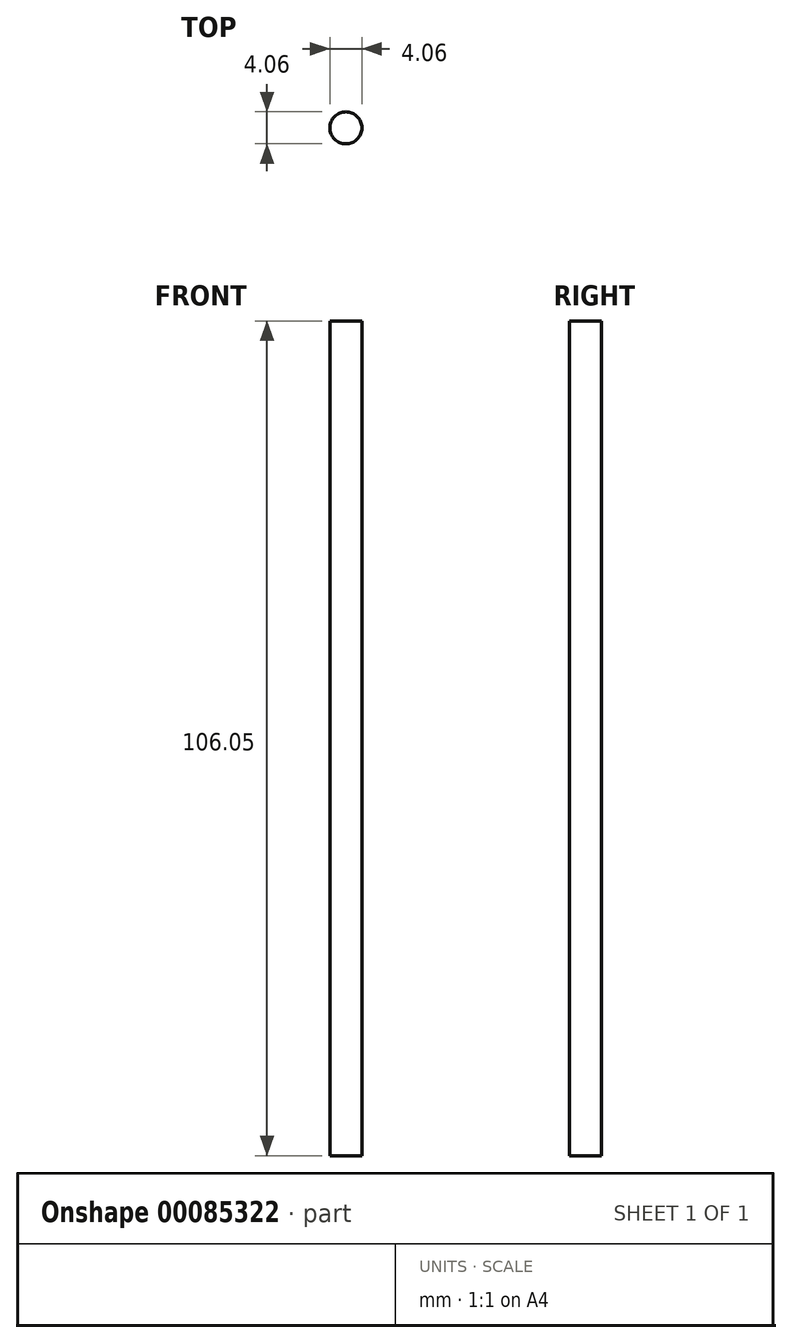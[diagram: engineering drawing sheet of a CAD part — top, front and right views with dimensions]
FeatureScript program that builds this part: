
annotation { "Feature Type Name" : "Feature", "Feature Type Description" : "" }
export const myFeature = defineFeature(function(context is Context, id is Id, definition is map)
    precondition{}
    {
        {
            var Q0;
            Q0=qCreatedBy(makeId("Top.planeOp"),FACE);
            var sketch = newSketch(context, id + "F0", { "sketchPlane" : qUnion([Q0])});
            skCircle(sketch, "E0", {"center": v(0, 0) * mm, "radius": 2.03 * mm});
            skSolve(sketch);
        }
        {
            var Q0;
            Q0 = qSketchRegion(id + "F0", true);
            extrude(context, id + "F1", {"entities" : qUnion([Q0]), "depth" : 106.04 * mm});
        }
    });
